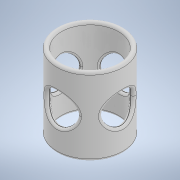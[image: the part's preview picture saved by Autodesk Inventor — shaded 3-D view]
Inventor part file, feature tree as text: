
AUTODESK INVENTOR PART (.ipt)
format: ipt  version: 2020 (Build 240168000, 168)  size: 522,240 bytes
history: native  units: in
note: dims shown in document units (in); Inventor stores cm internally (conversion verified against a paired STEP export)
features: extrude x3, sketch x3, fillet x2
ambient origin geometry x8: Origin, YZ Plane, XZ Plane, XY Plane, X Axis, Y Axis, Z Axis, Center Point
bodies: Solid1 (feature_tree)
feature tree (8):
  extrude  "Extrusion1"  Depth=0.1181in
  fillet  "Fillet1"  Radius=1.9685in
  extrude  "Extrusion2"  Depth=0.7874in
  extrude  "Extrusion3"  Depth=0.7874in
  fillet  "Fillet2"  Radius=1.9685in
  sketch  "Sketch1"  dims[d0=1.4567in d1=0.1181in d2=1.9685in d3=0.0in]
  sketch  "Sketch2"  dims[d4=0.0591in d5=0.7874in]
  sketch  "Sketch3"  dims[d6=1.9685in d7=0.0in d8=0.7874in d9=1.9685in d10=0.0in d11=0.0551in]
